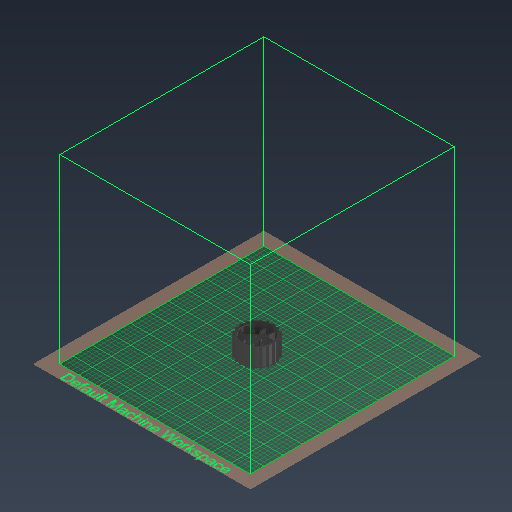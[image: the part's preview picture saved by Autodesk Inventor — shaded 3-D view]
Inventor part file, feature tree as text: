
AUTODESK INVENTOR PART (.ipt)
format: ipt  version: 2021 (Build 250183000, 183)  size: 972,288 bytes
history: native  units: mm
features: extrude x6, sketch x4, pattern_circular x1
ambient origin geometry x8: Origin, YZ Plane, XZ Plane, XY Plane, X Axis, Y Axis, Z Axis, Center Point
bodies: Body1 (feature_tree)
feature tree (11):
  sketch  "Skizze2"  dims[d2=70.0mm d3=3.0mm]
  extrude  "Extrusion5"  Depth=3.0mm
  extrude  "Extrusion7"  Depth=2.0mm
  extrude  "Extrusion8"  Depth=40.0mm TaperAngle=360.0deg
  extrude  "Extrusion9"  Depth=25.0mm TaperAngle=0.0deg
  extrude  "Extrusion11"  Depth=45.0mm TaperAngle=0.0deg
  pattern_circular  "Runde Anordnung1"  [2 undecoded]
  extrude  "Extrusion12"  Depth=0.5mm
  sketch  "Skizze3"  dims[d4=15.0mm d9=2.0mm]
  sketch  "Skizze9"  dims[d14=3.0mm d24=40.0mm d26=360.0deg]
  sketch  "Skizze10"  dims[d28=5.0mm d29=0.0mm d32=25.0mm d33=0.0mm d34=45.0mm d35=0.0mm d36=35.0mm d37=0.0mm d38=9.0mm d39=4.5mm d47=4.5mm d50=15.0mm d51=0.0mm d102=2.0mm d103=3.0mm d104=34.98mm d105=0.5mm d106=40.0mm d107=0.0mm d108=1.0mm d109=200.0mm d110=360.0deg d112=3.3mm d113=4.0mm d114=3.3865mm d115=5.0mm d116=13.0mm d117=0.0mm d15=0.5mm d16=0.872665mm d17=0.5mm d18=0.872665mm d43=0.5mm d44=0.872665mm d45=0.5mm d46=0.872665mm d66=1.0mm d67=1.0mm d68=1.0mm d69=0.15mm d70=0.25mm d71=0.375mm d72=14.3117mm d73=0.75mm d74=20.594885mm d75=0.0625mm d76=0.75mm d77=0.375mm]
note: 2 required parameter values undecoded (feature->parameter linkage not recoverable at this tier; creation-order binding heuristic only, values carry confidence <= 0.55)
